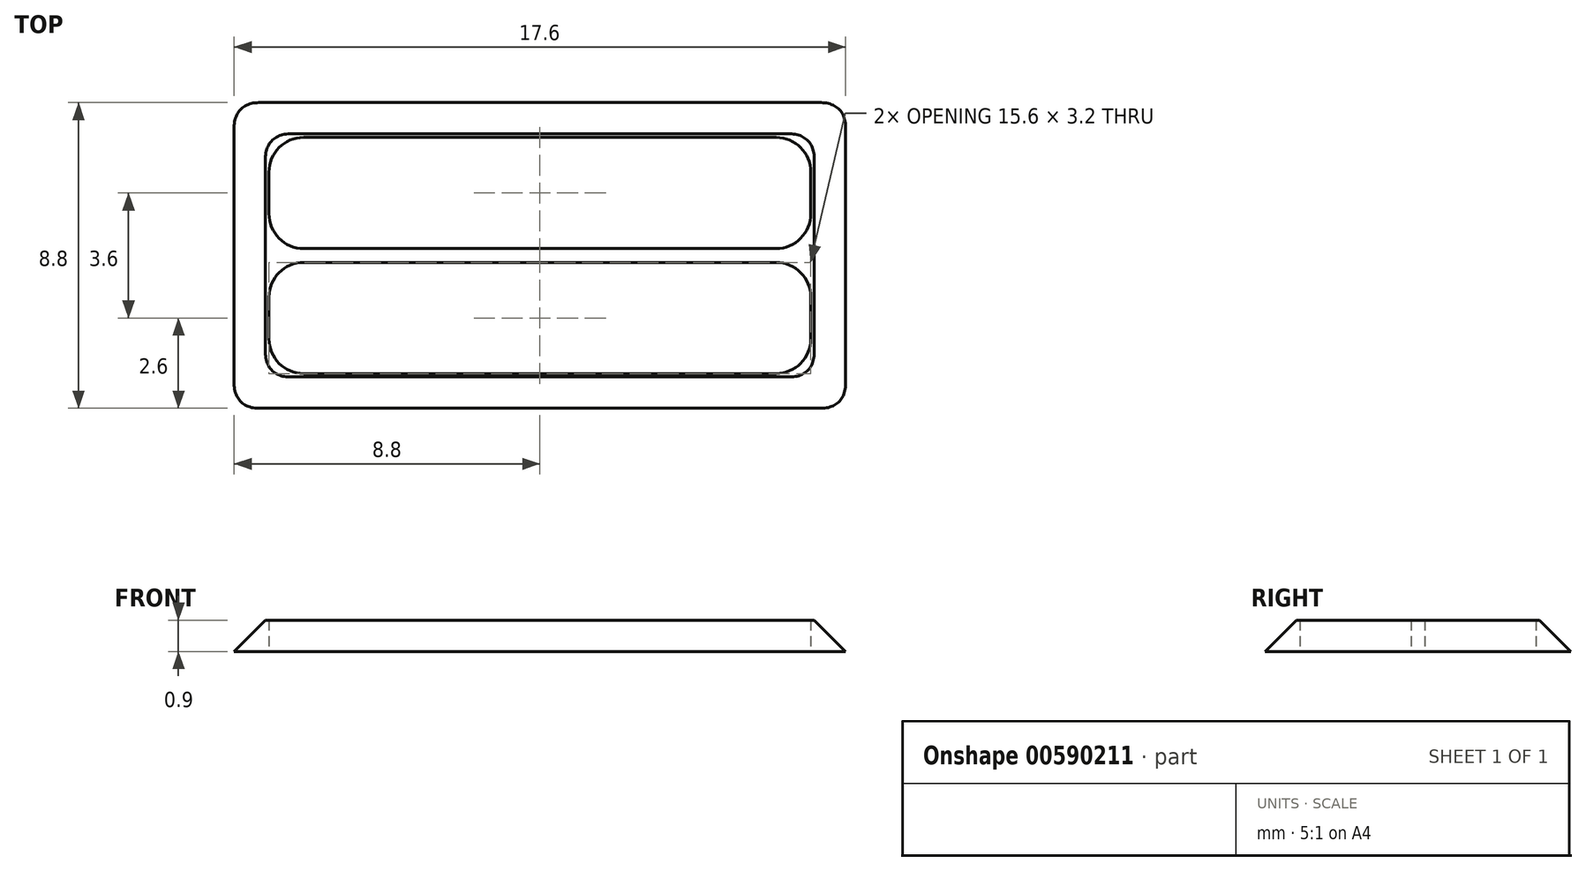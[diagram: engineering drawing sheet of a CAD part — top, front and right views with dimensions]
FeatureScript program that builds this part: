
annotation { "Feature Type Name" : "Feature", "Feature Type Description" : "" }
export const myFeature = defineFeature(function(context is Context, id is Id, definition is map)
    precondition{}
    {
        {
            var Q0;
            Q0=qCreatedBy(makeId("Top.planeOp"),FACE);
            var sketch = newSketch(context, id + "F0", { "sketchPlane" : qUnion([Q0])});
            skPoint(sketch, "E0.middle", {"position": v(0, 0) * mm});
            skLineSegment(sketch, "E1.bottom", {"start": v(-7.8, 3.4) * mm, "end": v(7.8, 3.4) * mm});
            skLineSegment(sketch, "E1.top", {"start": v(-7.8, 0.2) * mm, "end": v(7.8, 0.2) * mm});
            skLineSegment(sketch, "E1.left", {"start": v(-7.8, 3.4) * mm, "end": v(-7.8, 0.2) * mm});
            skLineSegment(sketch, "E1.right", {"start": v(7.8, 3.4) * mm, "end": v(7.8, 0.2) * mm});
            skPoint(sketch, "E1.middle", {"position": v(0, 1.8) * mm});
            skLineSegment(sketch, "E2.bottom", {"start": v(-7.8, -0.2) * mm, "end": v(7.8, -0.2) * mm});
            skLineSegment(sketch, "E2.top", {"start": v(-7.8, -3.4) * mm, "end": v(7.8, -3.4) * mm});
            skLineSegment(sketch, "E2.left", {"start": v(-7.8, -0.2) * mm, "end": v(-7.8, -3.4) * mm});
            skLineSegment(sketch, "E2.right", {"start": v(7.8, -0.2) * mm, "end": v(7.8, -3.4) * mm});
            skPoint(sketch, "E2.middle", {"position": v(0, -1.8) * mm});
            skLineSegment(sketch, "E3.bottom", {"start": v(-9, 4.6) * mm, "end": v(9, 4.6) * mm});
            skLineSegment(sketch, "E3.top", {"start": v(-9, -4.6) * mm, "end": v(9, -4.6) * mm});
            skLineSegment(sketch, "E3.left", {"start": v(-9, 4.6) * mm, "end": v(-9, -4.6) * mm});
            skLineSegment(sketch, "E3.right", {"start": v(9, 4.6) * mm, "end": v(9, -4.6) * mm});
            skSolve(sketch);
        }
        {
            var Q0;
            Q0=makeQuery(id+"F0.imprint","IMPRINT",FACE,{"disambiguationData":[TD([[makeQuery(id+"F0.imprint","IMPRINT",EDGE,{"derivedFrom":sQuery(id+"F0.wireOp",EDGE,"E1.bottom")}),1.0]])]});
            extrude(context, id + "F1", {"entities" : qUnion([Q0]), "depth" : .9 * mm, "offsetDistance" : 25 * mm});
        }
        {
            var Q0;
            Q0=makeQuery(id+"F1.opExtrude","CAP_EDGE",EDGE,{"disambiguationData":[OSD([sQuery(id+"F0.wireOp",EDGE,"E3.top")])],"isStart":false});
            var Q1;
            Q1=makeQuery(id+"F1.opExtrude","CAP_EDGE",EDGE,{"disambiguationData":[OSD([sQuery(id+"F0.wireOp",EDGE,"E3.left")])],"isStart":false});
            var Q2;
            Q2=makeQuery(id+"F1.opExtrude","CAP_EDGE",EDGE,{"disambiguationData":[OSD([sQuery(id+"F0.wireOp",EDGE,"E3.bottom")])],"isStart":false});
            var Q3;
            Q3=makeQuery(id+"F1.opExtrude","CAP_EDGE",EDGE,{"disambiguationData":[OSD([sQuery(id+"F0.wireOp",EDGE,"E3.right")])],"isStart":false});
            chamfer(context, id + "F2", {"entities" : qUnion([Q0, Q1, Q2, Q3]), "width" : 1.1 * mm, "tangentPropagation" : true});
        }
        {
            var Q0;
            Q0=makeQuery(id+"F1.opExtrude","SWEPT_EDGE",EDGE,{"disambiguationData":[OSD([sQuery(id+"F0.wireOp",EDGE,"E1.bottom"),sQuery(id+"F0.wireOp",EDGE,"E1.left")])]});
            var Q1;
            Q1=makeQuery(id+"F1.opExtrude","SWEPT_EDGE",EDGE,{"disambiguationData":[OSD([sQuery(id+"F0.wireOp",EDGE,"E2.bottom"),sQuery(id+"F0.wireOp",EDGE,"E2.left")])]});
            var Q2;
            Q2=makeQuery(id+"F1.opExtrude","SWEPT_EDGE",EDGE,{"disambiguationData":[OSD([sQuery(id+"F0.wireOp",EDGE,"E1.top"),sQuery(id+"F0.wireOp",EDGE,"E1.right")])]});
            var Q3;
            Q3=makeQuery(id+"F1.opExtrude","SWEPT_EDGE",EDGE,{"disambiguationData":[OSD([sQuery(id+"F0.wireOp",EDGE,"E2.top"),sQuery(id+"F0.wireOp",EDGE,"E2.right")])]});
            var Q4;
            Q4=makeQuery(id+"F1.opExtrude","SWEPT_EDGE",EDGE,{"disambiguationData":[OSD([sQuery(id+"F0.wireOp",EDGE,"E1.bottom"),sQuery(id+"F0.wireOp",EDGE,"E1.right")])]});
            var Q5;
            Q5=makeQuery(id+"F1.opExtrude","SWEPT_EDGE",EDGE,{"disambiguationData":[OSD([sQuery(id+"F0.wireOp",EDGE,"E2.bottom"),sQuery(id+"F0.wireOp",EDGE,"E2.right")])]});
            var Q6;
            Q6=makeQuery(id+"F1.opExtrude","SWEPT_EDGE",EDGE,{"disambiguationData":[OSD([sQuery(id+"F0.wireOp",EDGE,"E1.top"),sQuery(id+"F0.wireOp",EDGE,"E1.left")])]});
            var Q7;
            Q7=makeQuery(id+"F1.opExtrude","SWEPT_EDGE",EDGE,{"disambiguationData":[OSD([sQuery(id+"F0.wireOp",EDGE,"E2.top"),sQuery(id+"F0.wireOp",EDGE,"E2.left")])]});
            var Q8;
            Q8=makeQuery(id+"F2.opChamfer","BLEND_EDGE",EDGE,{"blendedFrom":[makeQuery(id+"F1.opExtrude","CAP_EDGE",EDGE,{"disambiguationData":[OSD([sQuery(id+"F0.wireOp",EDGE,"E3.top")])],"isStart":false}),makeQuery(id+"F1.opExtrude","CAP_EDGE",EDGE,{"disambiguationData":[OSD([sQuery(id+"F0.wireOp",EDGE,"E3.left")])],"isStart":false})],"blendedInto":[]});
            var Q9;
            Q9=makeQuery(id+"F2.opChamfer","BLEND_EDGE",EDGE,{"blendedFrom":[makeQuery(id+"F1.opExtrude","CAP_EDGE",EDGE,{"disambiguationData":[OSD([sQuery(id+"F0.wireOp",EDGE,"E3.top")])],"isStart":false}),makeQuery(id+"F1.opExtrude","CAP_EDGE",EDGE,{"disambiguationData":[OSD([sQuery(id+"F0.wireOp",EDGE,"E3.right")])],"isStart":false})],"blendedInto":[]});
            var Q10;
            Q10=makeQuery(id+"F2.opChamfer","BLEND_EDGE",EDGE,{"blendedFrom":[makeQuery(id+"F1.opExtrude","CAP_EDGE",EDGE,{"disambiguationData":[OSD([sQuery(id+"F0.wireOp",EDGE,"E3.bottom")])],"isStart":false}),makeQuery(id+"F1.opExtrude","CAP_EDGE",EDGE,{"disambiguationData":[OSD([sQuery(id+"F0.wireOp",EDGE,"E3.right")])],"isStart":false})],"blendedInto":[]});
            var Q11;
            Q11=makeQuery(id+"F2.opChamfer","BLEND_EDGE",EDGE,{"blendedFrom":[makeQuery(id+"F1.opExtrude","CAP_EDGE",EDGE,{"disambiguationData":[OSD([sQuery(id+"F0.wireOp",EDGE,"E3.bottom")])],"isStart":false}),makeQuery(id+"F1.opExtrude","CAP_EDGE",EDGE,{"disambiguationData":[OSD([sQuery(id+"F0.wireOp",EDGE,"E3.left")])],"isStart":false})],"blendedInto":[]});
            fillet(context, id + "F3", {"entities" : qUnion([Q0, Q1, Q2, Q3, Q4, Q5, Q6, Q7, Q8, Q9, Q10, Q11]), "radius" : 1 * mm, "tangentPropagation" : true, "allowEdgeOverflow" : false});
        }
    });
